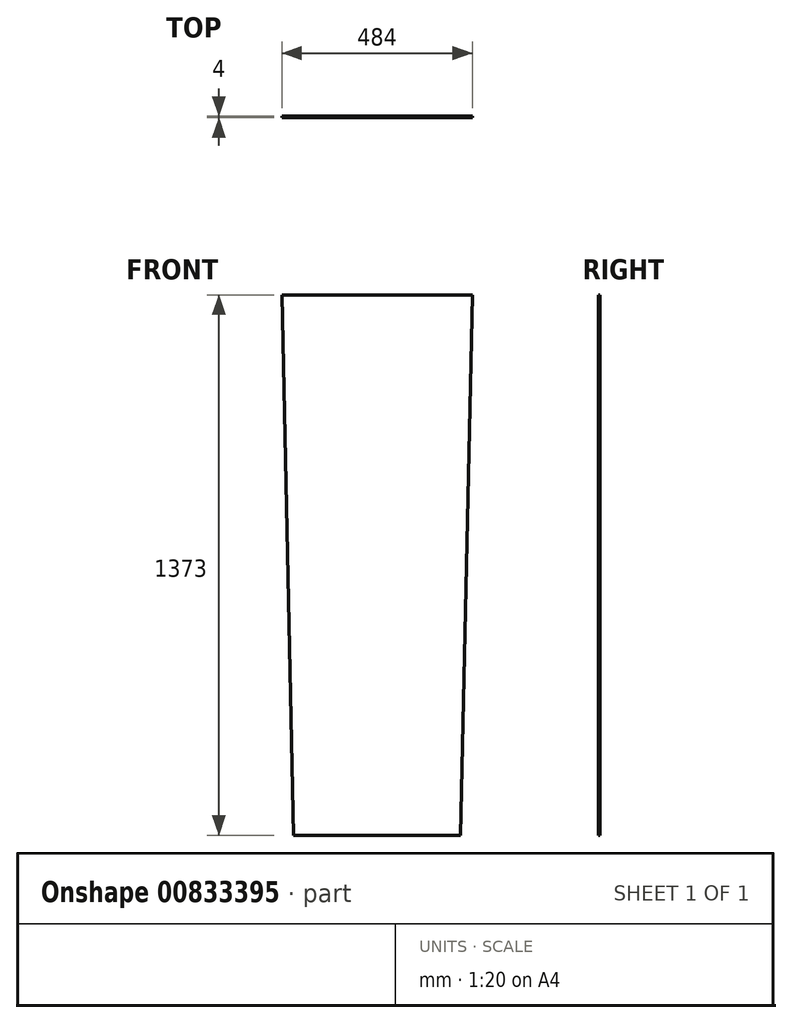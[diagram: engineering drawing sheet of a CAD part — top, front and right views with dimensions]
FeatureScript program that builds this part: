
annotation { "Feature Type Name" : "Feature", "Feature Type Description" : "" }
export const myFeature = defineFeature(function(context is Context, id is Id, definition is map)
    precondition{}
    {
        {
            var Q0;
            Q0=qCreatedBy(makeId("Front.planeOp"),FACE);
            var sketch = newSketch(context, id + "F0", { "sketchPlane" : qUnion([Q0])});
            skLineSegment(sketch, "E0", {"start": v(0, 0) * mm, "end": v(0, 1373) * mm, "construction": true});
            skLineSegment(sketch, "E1", {"start": v(0, 1373) * mm, "end": v(242, 1373) * mm});
            skLineSegment(sketch, "E2", {"start": v(242, 1373) * mm, "end": v(212.5, 0) * mm});
            skLineSegment(sketch, "E3", {"start": v(212.5, 0) * mm, "end": v(0, 0) * mm});
            skLineSegment(sketch, "E4.MirrorCS", {"start": v(-242, 1373) * mm, "end": v(-212.5, 0) * mm});
            skLineSegment(sketch, "E5.MirrorCS", {"start": v(0, 1373) * mm, "end": v(-242, 1373) * mm});
            skLineSegment(sketch, "E6.MirrorCS", {"start": v(-212.5, 0) * mm, "end": v(0, 0) * mm});
            skSolve(sketch);
        }
        {
            var Q0;
            Q0 = qSketchRegion(id + "F0", true);
            extrude(context, id + "F1", {"entities" : qUnion([Q0]), "depth" : 4 * mm, "offsetDistance" : 25 * mm});
        }
    });
